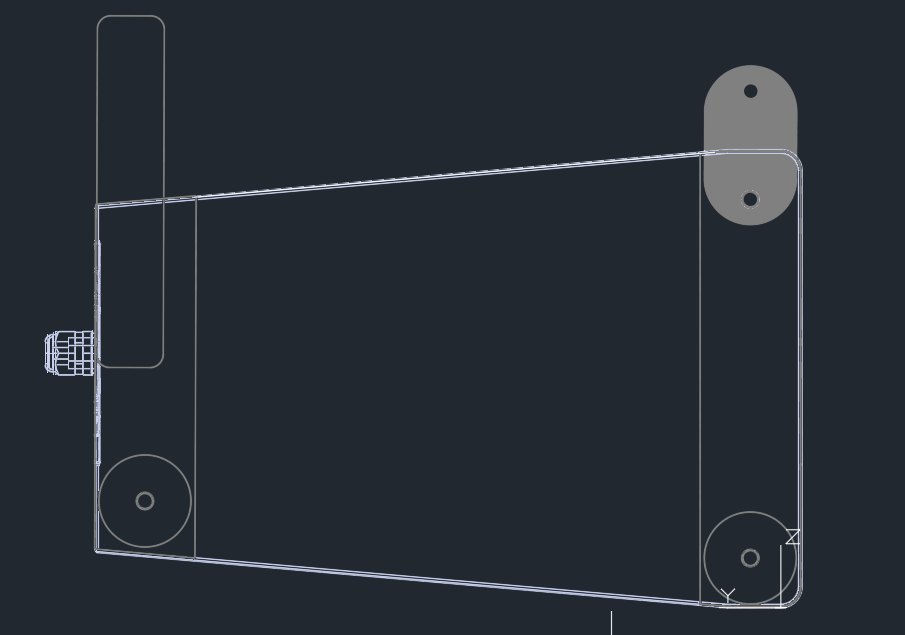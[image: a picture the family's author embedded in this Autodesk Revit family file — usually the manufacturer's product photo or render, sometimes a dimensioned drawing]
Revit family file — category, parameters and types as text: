
# Revit family: Communication_Bosch_Speakers_X-Line Advance Install X1i
name_source: partatom
category: Communication Devices
revit_build: Autodesk Revit 2018 (Build: 20180423_1000(x64)
units: mm (PartAtom-declared; Revit-internal decimal feet)

## family parameters
Always vertical = No
Cut with Voids When Loaded = No
Maintain Annotation Orientation = No
Part Type = Normal
Room Calculation Point = No
Round Connector Dimension = Use Diameter
Shared = Yes
Work Plane-Based = Yes

## types (8) — shared parameters
ArchitectsAndEngineersSpecs = https://products.electrovoice.com
Default Elevation = 1219 mm
Dimensions (H x W x D) = 347 mm x 678.5 mm x 536 mm
Disclaimer = https://resources-boschsecurity-cdn.azureedge.net
Frequency Response (-3 dB) = Full-space anechoic array performance with FIR-Drive
preset (57 Hz - 16 kHz)
Horizontal Coverage = 90° or 120°
IP Rating = IP55 (fiberglass models only)
InstallationManual = https://products.electrovoice.com
Manufacturer = Electro Voice
Material = Multi-ply birch
Max SPL = 143 dB Peak
PlanningTools = https://products.electrovoice.com
Power Handling = 500 W Continuous, 2000 Peak
Product Information = https://products.electrovoice.com
Product Website = https://products.electrovoice.com
URL = www.electrovoice.com
UniclassCode = Pr_70_75_36_50
UniclassTitle = Loudspeakers
Vertical Coverage = Array dependent
Weight (Kg) = 34.9
ifcExportAs = IfcElectricApplianceType

## per-type parameters (varying)
| type | Colour | XMTI |
| X1I-212/90-B X1i 12" 90° Install array black | RAL 9005 black | 5 |
| X1I-212/90-W X1i 12" 90° Install array white | RAL 9003 white | 8 |
| X1I-212/90-FGB X1i 12" 90° Install array black FG | RAL 9005 black | 6 |
| X1I-212/90-FGW X1i 12" 90° Install array white FG | RAL 9003 white | 7 |
| X1I-212/120-B X1i 12" 120° Install array black | RAL 9005 black | 1 |
| X1I-212/120-W X1i 12" 120° Install array white | RAL 9003 white | 4 |
| X1I-212/120-FGB X1i 12" 120° Install array black FG | RAL 9005 black | 2 |
| X1I-212/120-FGW X1i 12" 120° Install array white FG | RAL 9003 white | 3 |

## geometry (parser evidence)
native form markers: Sweep x20
no freeform markers — native parametric forms only
